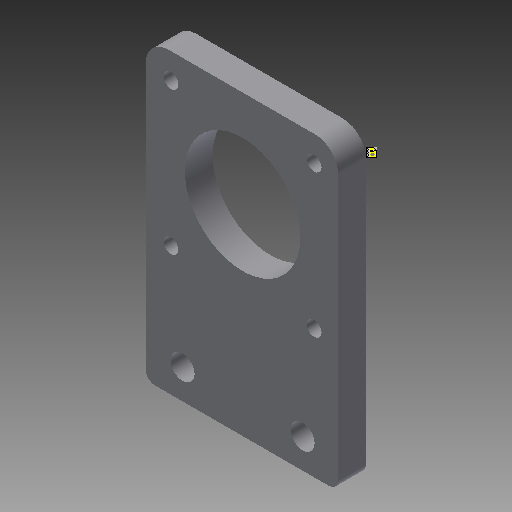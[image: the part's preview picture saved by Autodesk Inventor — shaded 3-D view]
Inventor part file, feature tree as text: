
AUTODESK INVENTOR PART (.ipt)
format: ipt  version: 2018 (Build 220112000, 112)  size: 161,792 bytes
history: native  units: mm
features: sketch x3, extrude x1
ambient origin geometry x8: Origin, YZ Plane, XZ Plane, XY Plane, X Axis, Y Axis, Z Axis, Center Point
bodies: Solid1 (feature_tree)
feature tree (4):
  sketch  "Sketch1"  dims[d8=3.2mm d9=3.2mm]
  sketch  "Sketch2"  dims[d10=5.5mm]
  sketch  "Sketch3"  dims[d13=5.2mm d14=5.2mm d16=2.0mm d17=40.0mm d18=90.0deg d19=20.0mm d22=20.0mm d23=10.0mm d24=8.5mm d25=6.0mm d26=0.0mm d27=2.0mm]
  extrude  "Extrusion1"  Depth=3.2mm
